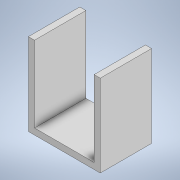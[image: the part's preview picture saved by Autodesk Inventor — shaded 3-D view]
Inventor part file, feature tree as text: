
AUTODESK INVENTOR PART (.ipt)
format: ipt  version: 2020 (Build 240168000, 168)  size: 104,960 bytes
history: native  units: mm
features: extrude x1, sketch x1
ambient origin geometry x8: Origin, YZ Plane, XZ Plane, XY Plane, X Axis, Y Axis, Z Axis, Center Point
bodies: Solid1 (feature_tree)
feature tree (2):
  extrude  "Extrusion1"  Depth=80.0mm
  sketch  "Sketch1"  dims[d0=70.0mm d1=80.0mm d2=80.0mm d3=6.0mm d4=50.0mm d5=0.0mm d6=0.5mm d7=0.872665mm]
